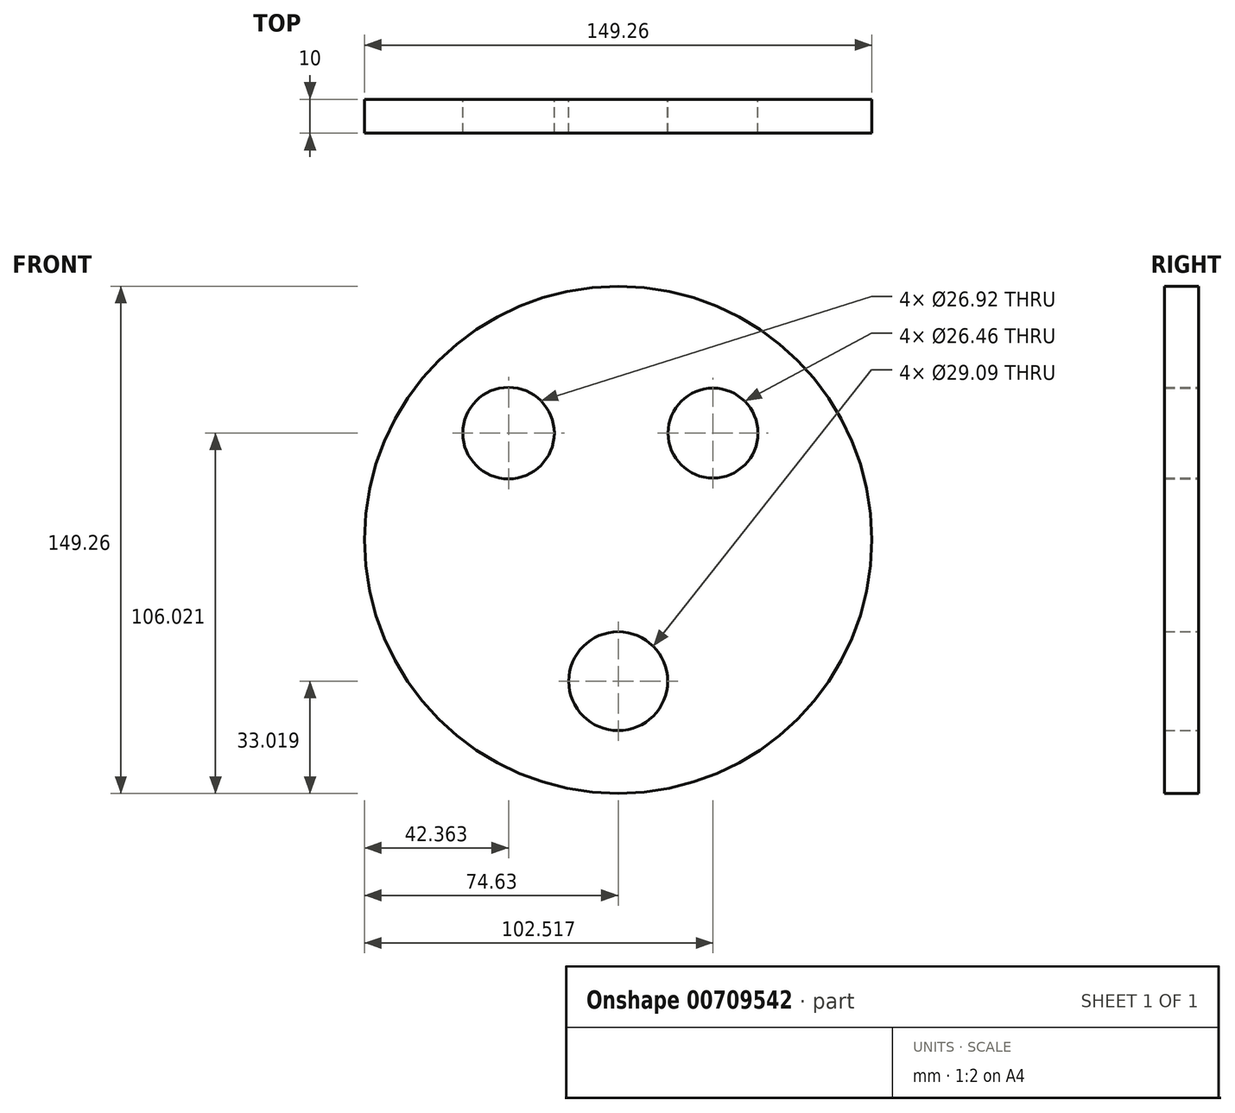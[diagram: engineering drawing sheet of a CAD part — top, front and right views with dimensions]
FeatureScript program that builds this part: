
annotation { "Feature Type Name" : "Feature", "Feature Type Description" : "" }
export const myFeature = defineFeature(function(context is Context, id is Id, definition is map)
    precondition{}
    {
        {
            var Q0;
            Q0=qCreatedBy(makeId("Front.planeOp"),FACE);
            var sketch = newSketch(context, id + "F0", { "sketchPlane" : qUnion([Q0])});
            skCircle(sketch, "E0", {"center": v(0, 0) * mm, "radius": 74.63 * mm});
            skCircle(sketch, "E1", {"center": v(-32.27, 31.4) * mm, "radius": 13.46 * mm});
            skCircle(sketch, "E2", {"center": v(27.89, 31.4) * mm, "radius": 13.23 * mm});
            skCircle(sketch, "E3", {"center": v(0, -41.61) * mm, "radius": 14.55 * mm});
            skSolve(sketch);
        }
        {
            var Q0;
            Q0=makeQuery(id+"F0.imprint","IMPRINT",FACE,{"disambiguationData":[TD([[makeQuery(id+"F0.imprint","IMPRINT",EDGE,{"derivedFrom":sQuery(id+"F0.wireOp",EDGE,"E0")}),1.0]])]});
            extrude(context, id + "F1", {"entities" : qUnion([Q0]), "depth" : 10 * mm, "offsetDistance" : 25.4 * mm});
        }
    });
